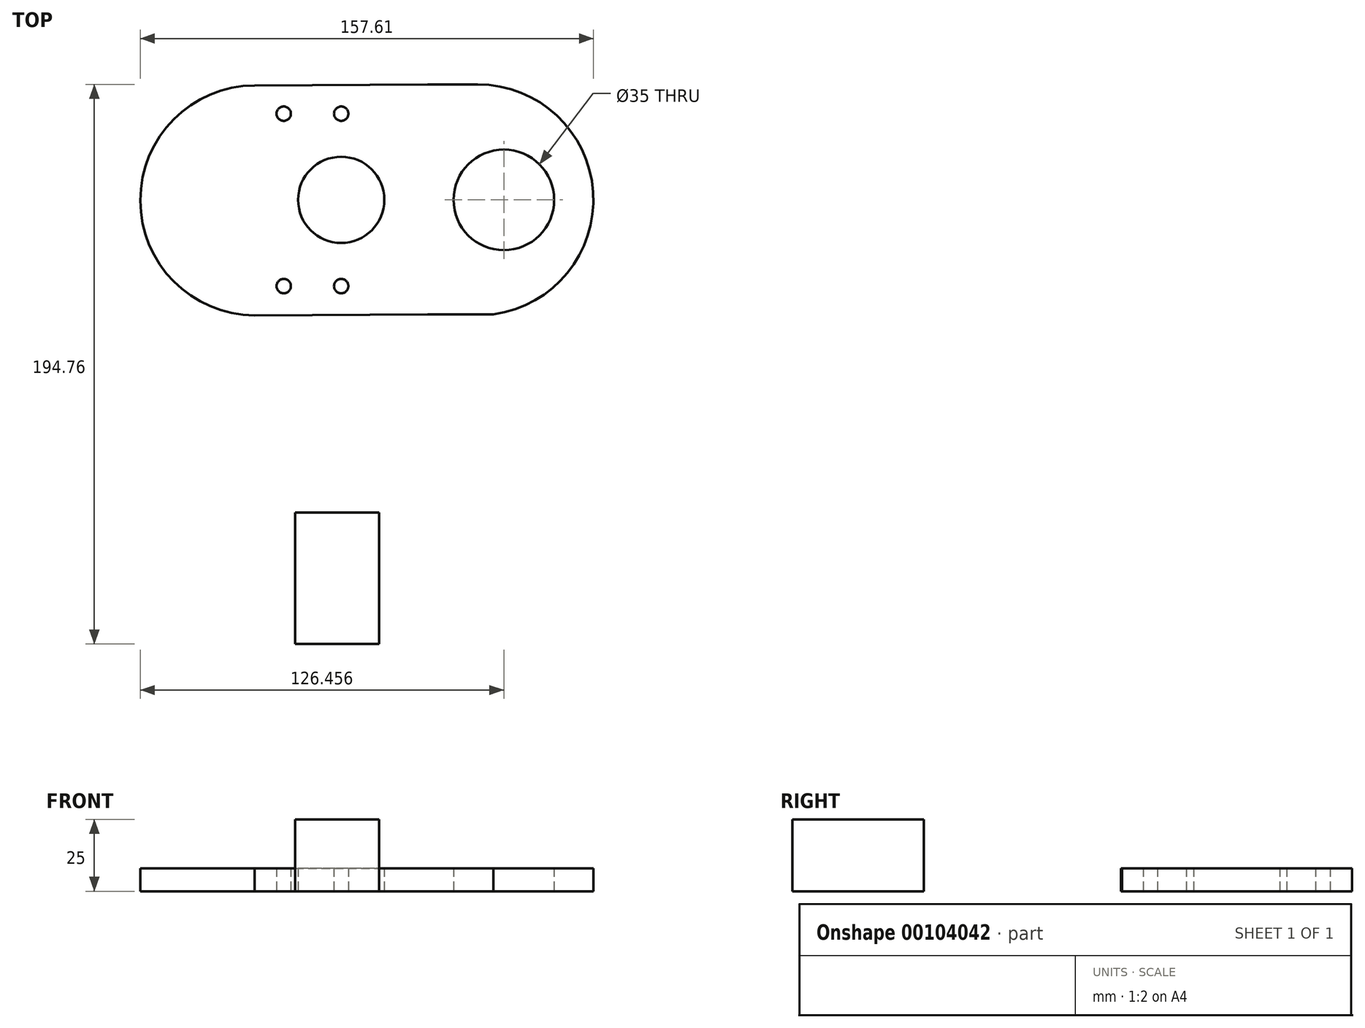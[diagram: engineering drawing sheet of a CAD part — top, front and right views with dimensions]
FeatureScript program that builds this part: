
annotation { "Feature Type Name" : "Feature", "Feature Type Description" : "" }
export const myFeature = defineFeature(function(context is Context, id is Id, definition is map)
    precondition{}
    {
        {
            var Q0;
            Q0=qCreatedBy(makeId("Top.planeOp"),FACE);
            var sketch = newSketch(context, id + "F0", { "sketchPlane" : qUnion([Q0])});
            skLineSegment(sketch, "E0.bottom", {"start": v(30.07, 40.18) * mm, "end": v(-30.07, 39.82) * mm});
            skPoint(sketch, "E0.middle", {"position": v(0, 0) * mm});
            skCircle(sketch, "E1", {"center": v(56.57, 0) * mm, "radius": 17.5 * mm});
            skCircle(sketch, "E2", {"center": v(0, 0) * mm, "radius": 15 * mm});
            skLineSegment(sketch, "E3", {"start": v(30.07, -39.82) * mm, "end": v(52.9, -39.82) * mm});
            skLineSegment(sketch, "E4", {"start": v(30.07, 40.18) * mm, "end": v(47.54, 40.18) * mm});
            skArc(sketch, "E5", {"start": v(52.9, -39.82) * mm, "mid": v(87.63, 2.69) * mm, "end": v(47.54, 40.18) * mm});
            skLineSegment(sketch, "E6.bottom", {"start": v(30.16, 30) * mm, "end": v(-30.16, 30) * mm, "construction": true});
            skLineSegment(sketch, "E6.top", {"start": v(30.16, -30) * mm, "end": v(-30.16, -30) * mm, "construction": true});
            skLineSegment(sketch, "E6.left", {"start": v(30.16, 30) * mm, "end": v(30.16, -30) * mm, "construction": true});
            skLineSegment(sketch, "E6.right", {"start": v(-30.16, 30) * mm, "end": v(-30.16, -30) * mm, "construction": true});
            skArc(sketch, "E7", {"start": v(-30.07, 39.82) * mm, "mid": v(-69.9, -0.18) * mm, "end": v(-30.07, -40.18) * mm});
            skLineSegment(sketch, "E8.0", {"start": v(30.08, 35.18) * mm, "end": v(-30.16, 34.82) * mm});
            skArc(sketch, "E8.3", {"start": v(-30.16, 34.82) * mm, "mid": v(-64.9, -0.31) * mm, "end": v(-29.9, -35.18) * mm});
            skArc(sketch, "E8.4", {"start": v(47.54, -35.18) * mm, "mid": v(82.72, 0) * mm, "end": v(47.54, 35.18) * mm});
            skLineSegment(sketch, "E8.5", {"start": v(30.08, 35.18) * mm, "end": v(47.54, 35.18) * mm});
            skLineSegment(sketch, "E9", {"start": v(-30.07, -40.18) * mm, "end": v(30.07, -39.82) * mm});
            skCircle(sketch, "E10", {"center": v(0, -30) * mm, "radius": 2.5 * mm});
            skCircle(sketch, "E11", {"center": v(-20, -30) * mm, "radius": 2.5 * mm});
            skLineSegment(sketch, "E12", {"start": v(0, 0) * mm, "end": v(30.16, 0) * mm, "construction": true});
            skCircle(sketch, "E13.MirrorC", {"center": v(0, 30) * mm, "radius": 2.5 * mm});
            skCircle(sketch, "E14.MirrorC", {"center": v(-20, 30) * mm, "radius": 2.5 * mm});
            skLineSegment(sketch, "E15.0", {"start": v(30.09, 33.68) * mm, "end": v(-30.03, 33.32) * mm, "construction": true});
            skArc(sketch, "E15.3", {"start": v(-30.03, 33.32) * mm, "mid": v(-63.4, -0.25) * mm, "end": v(-29.9, -33.68) * mm, "construction": true});
            skArc(sketch, "E15.4", {"start": v(47.54, -33.68) * mm, "mid": v(81.22, 0) * mm, "end": v(47.54, 33.68) * mm, "construction": true});
            skLineSegment(sketch, "E15.5", {"start": v(30.09, 33.68) * mm, "end": v(47.54, 33.68) * mm, "construction": true});
            skLineSegment(sketch, "E16", {"start": v(-29.9, -35.18) * mm, "end": v(47.54, -35.18) * mm});
            skLineSegment(sketch, "E17", {"start": v(47.54, -33.68) * mm, "end": v(-29.9, -33.68) * mm, "construction": true});
            skSolve(sketch);
        }
        {
            var Q0;
            Q0=makeQuery(id+"F0.imprint","IMPRINT",FACE,{"disambiguationData":[TD([[makeQuery(id+"F0.imprint","IMPRINT",EDGE,{"derivedFrom":sQuery(id+"F0.wireOp",EDGE,"E1")}),-1.0]])]});
            var Q1;
            Q1=makeQuery(id+"F0.imprint","IMPRINT",FACE,{"disambiguationData":[TD([[makeQuery(id+"F0.imprint","IMPRINT",EDGE,{"derivedFrom":sQuery(id+"F0.wireOp",EDGE,"E0.bottom")}),1.0]])]});
            extrude(context, id + "F1", {"entities" : qUnion([Q0, Q1]), "depth" : 8 * mm});
        }
        {
            var Q0;
            Q0=qCreatedBy(makeId("Top.planeOp"),FACE);
            var sketch = newSketch(context, id + "F2", { "sketchPlane" : qUnion([Q0])});
            skLineSegment(sketch, "E18", {"start": v(-16.08, -154.58) * mm, "end": v(13.13, -154.58) * mm});
            skLineSegment(sketch, "E19", {"start": v(13.13, -154.58) * mm, "end": v(13.13, -108.86) * mm});
            skLineSegment(sketch, "E20", {"start": v(13.13, -108.86) * mm, "end": v(-16.08, -108.86) * mm});
            skLineSegment(sketch, "E21", {"start": v(-16.08, -108.86) * mm, "end": v(-16.08, -154.58) * mm});
            skArc(sketch, "E22", {"start": v(14.6, -22.96) * mm, "mid": v(14.6, -22.96) * mm, "end": v(14.6, -22.96) * mm});
            skArc(sketch, "E23", {"start": v(-14.6, -22.96) * mm, "mid": v(-17.55, -286.2) * mm, "end": v(-14.6, -22.96) * mm});
            skArc(sketch, "E24", {"start": v(14.7, 22.86) * mm, "mid": v(14.6, 22.86) * mm, "end": v(14.5, 22.86) * mm});
            skArc(sketch, "E25", {"start": v(14.5, -22.86) * mm, "mid": v(11.66, -286.3) * mm, "end": v(14.7, -22.86) * mm});
            skArc(sketch, "E26", {"start": v(14.6, 22.76) * mm, "mid": v(14.6, 22.76) * mm, "end": v(14.6, 22.76) * mm});
            skArc(sketch, "E27", {"start": v(-14.5, 22.86) * mm, "mid": v(-14.6, 22.86) * mm, "end": v(-14.7, 22.86) * mm});
            skArc(sketch, "E28", {"start": v(9.18, -3.81) * mm, "mid": v(6.27, -267.25) * mm, "end": v(9.25, -3.81) * mm});
            skArc(sketch, "E29", {"start": v(-7.02, -3.81) * mm, "mid": v(-9.93, -267.25) * mm, "end": v(-6.95, -3.81) * mm});
            skArc(sketch, "E30", {"start": v(9.21, -3.84) * mm, "mid": v(9.21, -3.84) * mm, "end": v(9.21, -3.84) * mm});
            skArc(sketch, "E31", {"start": v(-6.99, -3.84) * mm, "mid": v(-9.93, -267.22) * mm, "end": v(-6.99, -3.84) * mm});
            skLineSegment(sketch, "E32", {"start": v(-0.08, -152.04) * mm, "end": v(-1.59, -152.04) * mm});
            skArc(sketch, "E33", {"start": v(-0.12, -20.57) * mm, "mid": v(-3.06, -283.5) * mm, "end": v(-0.12, -20.57) * mm});
            skArc(sketch, "E34", {"start": v(1.39, -20.57) * mm, "mid": v(1.39, -20.57) * mm, "end": v(1.38, -20.57) * mm});
            skLineSegment(sketch, "E35", {"start": v(-0.08, -149.5) * mm, "end": v(-1.59, -149.5) * mm});
            skArc(sketch, "E36", {"start": v(-0.12, -18.03) * mm, "mid": v(-3.06, -280.97) * mm, "end": v(-0.12, -18.03) * mm});
            skArc(sketch, "E37", {"start": v(1.39, -18.03) * mm, "mid": v(1.39, -18.03) * mm, "end": v(1.38, -18.03) * mm});
            skLineSegment(sketch, "E38", {"start": v(-0.08, -146.96) * mm, "end": v(-1.59, -146.96) * mm});
            skArc(sketch, "E39", {"start": v(-0.12, -15.49) * mm, "mid": v(-3.06, -278.43) * mm, "end": v(-0.12, -15.49) * mm});
            skArc(sketch, "E40", {"start": v(1.39, -15.49) * mm, "mid": v(1.39, -15.49) * mm, "end": v(1.38, -15.49) * mm});
            skLineSegment(sketch, "E41", {"start": v(-0.08, -144.42) * mm, "end": v(-1.59, -144.42) * mm});
            skArc(sketch, "E42", {"start": v(-0.12, -12.95) * mm, "mid": v(-3.06, -275.89) * mm, "end": v(-0.12, -12.95) * mm});
            skArc(sketch, "E43", {"start": v(1.39, -12.95) * mm, "mid": v(1.39, -12.95) * mm, "end": v(1.38, -12.95) * mm});
            skLineSegment(sketch, "E44", {"start": v(-0.08, -141.88) * mm, "end": v(-1.59, -141.88) * mm});
            skArc(sketch, "E45", {"start": v(-0.12, -10.4) * mm, "mid": v(-3.06, -273.35) * mm, "end": v(-0.12, -10.4) * mm});
            skArc(sketch, "E46", {"start": v(1.39, -10.4) * mm, "mid": v(1.39, -10.4) * mm, "end": v(1.38, -10.4) * mm});
            skLineSegment(sketch, "E47", {"start": v(-0.84, -141.88) * mm, "end": v(-3.88, -141.88) * mm});
            skArc(sketch, "E48", {"start": v(0.64, -10.26) * mm, "mid": v(0.63, -10.26) * mm, "end": v(0.63, -10.26) * mm});
            skLineSegment(sketch, "E49", {"start": v(-3.88, -141.88) * mm, "end": v(-7.19, -141.88) * mm});
            skArc(sketch, "E50", {"start": v(-5.72, -10.26) * mm, "mid": v(-8.66, -273.5) * mm, "end": v(-5.71, -10.26) * mm});
            skArc(sketch, "E51", {"start": v(-2.4, -10.26) * mm, "mid": v(-2.4, -10.26) * mm, "end": v(-2.4, -10.26) * mm});
            skLineSegment(sketch, "E52", {"start": v(-7.19, -141.88) * mm, "end": v(-8.46, -141.88) * mm});
            skArc(sketch, "E53", {"start": v(-6.99, -10.26) * mm, "mid": v(-9.93, -273.5) * mm, "end": v(-6.98, -10.26) * mm});
            skArc(sketch, "E54", {"start": v(-5.71, -10.26) * mm, "mid": v(-5.72, -10.26) * mm, "end": v(-5.72, -10.26) * mm});
            skLineSegment(sketch, "E55", {"start": v(-8.46, -141.88) * mm, "end": v(-8.46, -137.3) * mm});
            skArc(sketch, "E56", {"start": v(-6.88, -5.58) * mm, "mid": v(-6.99, -5.58) * mm, "end": v(-7.09, -5.58) * mm});
            skArc(sketch, "E57", {"start": v(-7.09, -10.16) * mm, "mid": v(-9.93, -273.6) * mm, "end": v(-6.88, -10.16) * mm});
            skLineSegment(sketch, "E58", {"start": v(-8.46, -137.3) * mm, "end": v(-8.46, -133.53) * mm});
            skArc(sketch, "E59", {"start": v(-6.88, -1.81) * mm, "mid": v(-6.99, -1.81) * mm, "end": v(-7.09, -1.81) * mm});
            skLineSegment(sketch, "E60", {"start": v(-8.46, -133.53) * mm, "end": v(-9.19, -133.53) * mm});
            skArc(sketch, "E61", {"start": v(-6.98, -1.91) * mm, "mid": v(-6.99, -1.91) * mm, "end": v(-6.99, -1.91) * mm});
            skLineSegment(sketch, "E62", {"start": v(-9.19, -133.53) * mm, "end": v(-9.19, -134.26) * mm});
            skArc(sketch, "E63", {"start": v(-7.82, -2.54) * mm, "mid": v(-10.66, -265.98) * mm, "end": v(-7.61, -2.54) * mm});
            skArc(sketch, "E64", {"start": v(-7.61, -1.81) * mm, "mid": v(-7.72, -1.81) * mm, "end": v(-7.82, -1.81) * mm});
            skLineSegment(sketch, "E65", {"start": v(-9.19, -134.26) * mm, "end": v(-11, -134.26) * mm});
            skArc(sketch, "E66", {"start": v(-9.53, -2.64) * mm, "mid": v(-12.47, -265.88) * mm, "end": v(-9.52, -2.64) * mm});
            skArc(sketch, "E67", {"start": v(-7.71, -2.64) * mm, "mid": v(-7.72, -2.64) * mm, "end": v(-7.72, -2.64) * mm});
            skLineSegment(sketch, "E68", {"start": v(-11, -134.26) * mm, "end": v(-11, -131.72) * mm});
            skArc(sketch, "E69", {"start": v(-9.42, 0) * mm, "mid": v(-9.53, 0) * mm, "end": v(-9.63, 0) * mm});
            skArc(sketch, "E70", {"start": v(-9.63, -2.54) * mm, "mid": v(-12.47, -265.98) * mm, "end": v(-9.42, -2.54) * mm});
            skLineSegment(sketch, "E71", {"start": v(-11, -131.72) * mm, "end": v(-11, -124.1) * mm});
            skArc(sketch, "E72", {"start": v(-9.42, 7.62) * mm, "mid": v(-9.53, 7.62) * mm, "end": v(-9.63, 7.62) * mm});
            skArc(sketch, "E73", {"start": v(-9.63, 0) * mm, "mid": v(-12.47, -263.44) * mm, "end": v(-9.42, 0) * mm});
            skLineSegment(sketch, "E74", {"start": v(-11, -124.1) * mm, "end": v(-11, -121.56) * mm});
            skArc(sketch, "E75", {"start": v(-9.42, 10.16) * mm, "mid": v(-9.53, 10.16) * mm, "end": v(-9.63, 10.16) * mm});
            skArc(sketch, "E76", {"start": v(-9.63, 7.62) * mm, "mid": v(-12.47, -255.82) * mm, "end": v(-9.42, 7.62) * mm});
            skLineSegment(sketch, "E77", {"start": v(-11, -121.56) * mm, "end": v(-8.46, -121.56) * mm});
            skArc(sketch, "E78", {"start": v(-6.98, 10.06) * mm, "mid": v(-6.99, 10.06) * mm, "end": v(-6.99, 10.06) * mm});
            skLineSegment(sketch, "E79", {"start": v(-8.46, -121.56) * mm, "end": v(-8.46, -121.53) * mm});
            skArc(sketch, "E80", {"start": v(-6.88, 10.19) * mm, "mid": v(-6.99, 10.19) * mm, "end": v(-7.09, 10.2) * mm});
            skLineSegment(sketch, "E81", {"start": v(-8.46, -121.56) * mm, "end": v(-8.46, -123.53) * mm});
            skArc(sketch, "E82", {"start": v(-7.09, 8.2) * mm, "mid": v(-9.93, -255.25) * mm, "end": v(-6.88, 8.19) * mm});
            skArc(sketch, "E83", {"start": v(-6.88, 10.16) * mm, "mid": v(-6.99, 10.16) * mm, "end": v(-7.09, 10.16) * mm});
            skLineSegment(sketch, "E84", {"start": v(-0.84, -149.5) * mm, "end": v(8.05, -149.5) * mm});
            skArc(sketch, "E85", {"start": v(9.53, -17.88) * mm, "mid": v(9.52, -17.88) * mm, "end": v(9.52, -17.88) * mm});
            skArc(sketch, "E86", {"start": v(0.63, -17.88) * mm, "mid": v(-2.3, -281.12) * mm, "end": v(0.64, -17.88) * mm});
            skLineSegment(sketch, "E87", {"start": v(8.05, -149.5) * mm, "end": v(8.05, -148.23) * mm});
            skArc(sketch, "E88", {"start": v(9.63, -16.51) * mm, "mid": v(9.52, -16.51) * mm, "end": v(9.42, -16.5) * mm});
            skArc(sketch, "E89", {"start": v(9.42, -17.78) * mm, "mid": v(6.58, -281.22) * mm, "end": v(9.63, -17.78) * mm});
            skLineSegment(sketch, "E90", {"start": v(8.05, -148.23) * mm, "end": v(8.05, -146.96) * mm});
            skArc(sketch, "E91", {"start": v(9.63, -15.24) * mm, "mid": v(9.52, -15.24) * mm, "end": v(9.42, -15.24) * mm});
            skLineSegment(sketch, "E92", {"start": v(8.05, -141.88) * mm, "end": v(8.05, -140.6) * mm});
            skArc(sketch, "E93", {"start": v(9.63, -8.9) * mm, "mid": v(9.52, -8.9) * mm, "end": v(9.42, -8.9) * mm});
            skArc(sketch, "E94", {"start": v(9.42, -10.16) * mm, "mid": v(6.58, -273.6) * mm, "end": v(9.63, -10.16) * mm});
            skLineSegment(sketch, "E95", {"start": v(8.05, -140.6) * mm, "end": v(8.05, -138.38) * mm});
            skArc(sketch, "E96", {"start": v(9.63, -6.66) * mm, "mid": v(9.52, -6.66) * mm, "end": v(9.42, -6.66) * mm});
            skArc(sketch, "E97", {"start": v(9.52, -6.66) * mm, "mid": v(9.37, -6.66) * mm, "end": v(9.21, -6.66) * mm});
            skArc(sketch, "E98", {"start": v(9.42, -6.66) * mm, "mid": v(6.58, -270.1) * mm, "end": v(9.63, -6.66) * mm});
            skLineSegment(sketch, "E99", {"start": v(7.74, -138.07) * mm, "end": v(7.74, -133.53) * mm});
            skArc(sketch, "E100", {"start": v(9.32, -1.81) * mm, "mid": v(9.21, -1.81) * mm, "end": v(9.11, -1.81) * mm});
            skLineSegment(sketch, "E101", {"start": v(-0.84, -146.96) * mm, "end": v(-5.4, -146.96) * mm});
            skArc(sketch, "E102", {"start": v(0.64, -15.34) * mm, "mid": v(0.63, -15.34) * mm, "end": v(0.63, -15.34) * mm});
            skLineSegment(sketch, "E103", {"start": v(-5.4, -146.96) * mm, "end": v(-13.54, -146.96) * mm});
            skArc(sketch, "E104", {"start": v(-3.93, -15.34) * mm, "mid": v(-3.93, -15.34) * mm, "end": v(-3.94, -15.34) * mm});
            skLineSegment(sketch, "E105", {"start": v(-13.54, -146.96) * mm, "end": v(-13.54, -138.83) * mm});
            skArc(sketch, "E106", {"start": v(-11.96, -7.11) * mm, "mid": v(-12.07, -7.1) * mm, "end": v(-12.17, -7.1) * mm});
            skArc(sketch, "E107", {"start": v(-12.17, -15.24) * mm, "mid": v(-15, -278.68) * mm, "end": v(-11.96, -15.24) * mm});
            skLineSegment(sketch, "E108", {"start": v(-13.54, -138.83) * mm, "end": v(-13.54, -115.2) * mm});
            skArc(sketch, "E109", {"start": v(-11.96, 16.5) * mm, "mid": v(-12.07, 16.5) * mm, "end": v(-12.17, 16.5) * mm});
            skLineSegment(sketch, "E110", {"start": v(-13.54, -115.2) * mm, "end": v(-13.54, -110.13) * mm});
            skArc(sketch, "E111", {"start": v(-11.96, 21.59) * mm, "mid": v(-12.07, 21.59) * mm, "end": v(-12.17, 21.59) * mm});
            skArc(sketch, "E112", {"start": v(-12.17, 16.5) * mm, "mid": v(-15, -246.93) * mm, "end": v(-11.96, 16.5) * mm});
            skLineSegment(sketch, "E113", {"start": v(-13.54, -110.13) * mm, "end": v(-8.46, -110.13) * mm});
            skArc(sketch, "E114", {"start": v(-6.98, 21.49) * mm, "mid": v(-6.99, 21.49) * mm, "end": v(-6.99, 21.49) * mm});
            skLineSegment(sketch, "E115", {"start": v(-8.46, -110.13) * mm, "end": v(8.05, -110.13) * mm});
            skArc(sketch, "E116", {"start": v(9.53, 21.49) * mm, "mid": v(9.52, 21.49) * mm, "end": v(9.52, 21.49) * mm});
            skLineSegment(sketch, "E117", {"start": v(8.05, -110.13) * mm, "end": v(10.6, -110.13) * mm});
            skArc(sketch, "E118", {"start": v(12.07, 21.49) * mm, "mid": v(12.06, 21.49) * mm, "end": v(12.06, 21.49) * mm});
            skLineSegment(sketch, "E119", {"start": v(10.6, -110.13) * mm, "end": v(10.6, -112.67) * mm});
            skArc(sketch, "E120", {"start": v(11.96, 19.05) * mm, "mid": v(9.12, -244.39) * mm, "end": v(12.17, 19.05) * mm});
            skArc(sketch, "E121", {"start": v(12.17, 21.59) * mm, "mid": v(12.06, 21.59) * mm, "end": v(11.96, 21.59) * mm});
            skLineSegment(sketch, "E122", {"start": v(10.6, -112.67) * mm, "end": v(10.6, -119.33) * mm});
            skArc(sketch, "E123", {"start": v(12.17, 19.05) * mm, "mid": v(12.06, 19.05) * mm, "end": v(11.96, 19.05) * mm});
            skLineSegment(sketch, "E124", {"start": v(10.6, -119.33) * mm, "end": v(7.74, -119.53) * mm});
            skArc(sketch, "E125", {"start": v(12.07, 12.29) * mm, "mid": v(12.06, 12.29) * mm, "end": v(12.06, 12.29) * mm});
            skLineSegment(sketch, "E126", {"start": v(-0.84, -144.42) * mm, "end": v(6.58, -144.42) * mm});
            skArc(sketch, "E127", {"start": v(8.05, -12.8) * mm, "mid": v(8.05, -12.8) * mm, "end": v(8.05, -12.8) * mm});
            skArc(sketch, "E128", {"start": v(0.63, -12.8) * mm, "mid": v(-2.3, -276.04) * mm, "end": v(0.64, -12.8) * mm});
            skLineSegment(sketch, "E129", {"start": v(6.58, -144.42) * mm, "end": v(9.32, -144.42) * mm});
            skArc(sketch, "E130", {"start": v(10.8, -12.8) * mm, "mid": v(10.8, -12.8) * mm, "end": v(10.8, -12.8) * mm});
            skLineSegment(sketch, "E131", {"start": v(9.32, -144.42) * mm, "end": v(10.6, -144.42) * mm});
            skArc(sketch, "E132", {"start": v(12.07, -12.8) * mm, "mid": v(12.06, -12.8) * mm, "end": v(12.06, -12.8) * mm});
            skArc(sketch, "E133", {"start": v(10.8, -12.8) * mm, "mid": v(7.85, -276.04) * mm, "end": v(10.8, -12.8) * mm});
            skLineSegment(sketch, "E134", {"start": v(10.6, -144.42) * mm, "end": v(10.6, -140.4) * mm});
            skArc(sketch, "E135", {"start": v(12.17, -8.69) * mm, "mid": v(12.06, -8.68) * mm, "end": v(11.96, -8.68) * mm});
            skArc(sketch, "E136", {"start": v(11.96, -12.7) * mm, "mid": v(9.12, -276.14) * mm, "end": v(12.17, -12.7) * mm});
            skLineSegment(sketch, "E137", {"start": v(10.6, -140.4) * mm, "end": v(10.6, -121.56) * mm});
            skArc(sketch, "E138", {"start": v(12.17, 10.16) * mm, "mid": v(12.06, 10.16) * mm, "end": v(11.96, 10.16) * mm});
            skLineSegment(sketch, "E139", {"start": v(10.6, -121.56) * mm, "end": v(10.28, -121.56) * mm});
            skArc(sketch, "E140", {"start": v(11.75, 10.06) * mm, "mid": v(8.81, -253.18) * mm, "end": v(11.76, 10.06) * mm});
            skArc(sketch, "E141", {"start": v(12.07, 10.06) * mm, "mid": v(12.06, 10.06) * mm, "end": v(12.06, 10.06) * mm});
            skLineSegment(sketch, "E142", {"start": v(10.28, -121.56) * mm, "end": v(7.74, -121.53) * mm});
            skArc(sketch, "E143", {"start": v(9.21, 10.09) * mm, "mid": v(9.21, 10.09) * mm, "end": v(9.21, 10.09) * mm});
            skSolve(sketch);
        }
        {
            var Q0;
            Q0=makeQuery(id+"F2.imprint","IMPRINT",FACE,{"disambiguationData":[TD([[makeQuery(id+"F2.imprint","IMPRINT",EDGE,{"derivedFrom":sQuery(id+"F2.wireOp",EDGE,"E18")}),1.0]])]});
            extrude(context, id + "F3", {"entities" : qUnion([Q0]), "depth" : 25 * mm});
        }
    });
